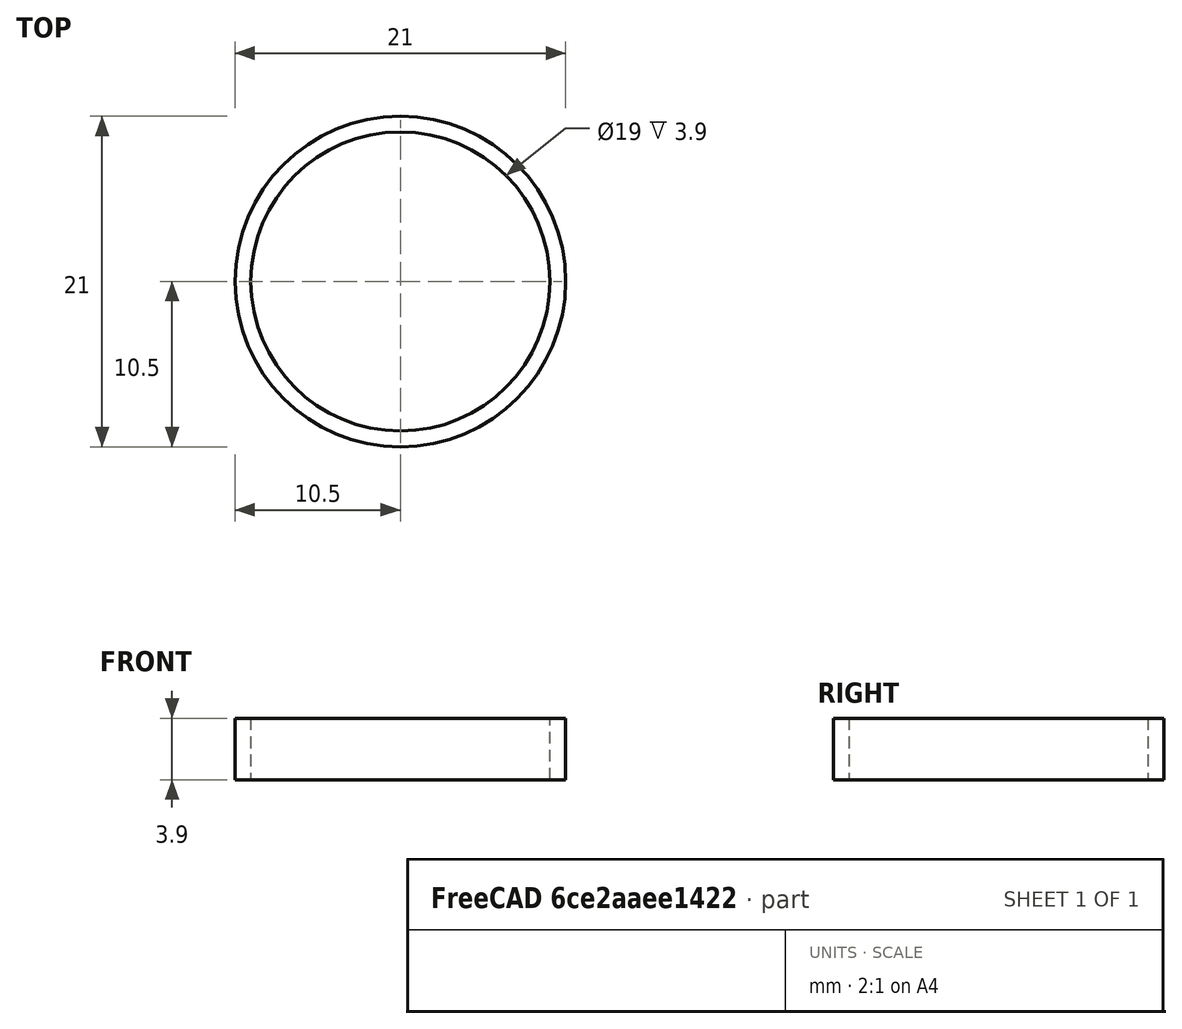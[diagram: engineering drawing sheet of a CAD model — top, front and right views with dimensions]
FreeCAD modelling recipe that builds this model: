
FCSTD DOCUMENT  (FreeCAD 0.20R)
Label: SnakeBot_Joint
License: All rights reserved
LicenseURL: http://en.wikipedia.org/wiki/All_rights_reserved
objects: Sketcher::SketchObject×1, PartDesign::Pad×1, PartDesign::Body×1, Mesh::Feature×1
note: 4 computed .brp shape members not serialized (recipe doc carries the construction recipe); baked Part::Feature solids carry a one-line shape summary decoded from their .brp

FEATURE [Sketcher::SketchObject] Sketch
  FullyConstrained = true
  MapMode = 5
  Support = -> [XY_Plane]
  sketch-geometry (2):
    g0: Circle CenterX=0 CenterY=0 CenterZ=0 NormalX=0 NormalY=0 NormalZ=1 AngleXU=0 Radius=9.5
    g1: Circle CenterX=0 CenterY=0 CenterZ=0 NormalX=0 NormalY=0 NormalZ=1 AngleXU=0 Radius=10.5
  constraints (4):
    c: Coincident(g0,g-1)
    c: Coincident(g1,g0)
    c: Diameter(g1) = 21
    c: Diameter(g0) = 19
FEATURE [PartDesign::Pad] Pad
  Direction = (0,0,1)
  Length = 3.9
  Length2 = 10
  Profile = -> Sketch
  ReferenceAxis = -> Sketch [N_Axis]
  Type = 0
FEATURE [PartDesign::Body] Body
  Group = -> [Sketch,Pad]
  Origin = -> Origin
  Tip = -> Pad
FEATURE [Mesh::Feature] SnakeBot_Wheel_Body  label="SnakeBot_Wheel-Body"
  Placement = pos=(0,0,5.5) rot=(0,0,1;0rad)
